# Revit family: Access_Flooring-FreeAxez-Border-L_Type
name_source: partatom
category: Specialty Equipment
units: mm (PartAtom-declared; Revit-internal decimal feet)

## family parameters
Always vertical = Yes
Classification Number = 23.35.50.27.14
Cut with Voids When Loaded = No
Enable Cutting in Views = No
Maintain Annotation Orientation = No
Part Type = Normal
Room Calculation Point = No
Round Connector Dimension = Use Diameter
Shared = No
Work Plane-Based = No

## types (2) — shared parameters
Default Elevation = 0' - 0"
Depth = 0' - 4 17/32"
Disclaimer = Your use of file(s) issued by FreeAxez, LLC confirms your acceptance of the following terms:  i) This file(s) is uncontrolled.  ii) Drawings are issued from FreeAxez, LLC in PDF format: The PDF document contains the issued data. Any accompanying BIM, CAD, image, or supplementary support file(s) is issued for your information only. Where discrepancies arise, the PDF document will take priority.  iii) This file(s) is to assist you with your production of work commissioned by FreeAxez, LLC for FreeAxez, LLC for the current project only and is not to be reused or manipulated by you on other projects, nor is it to be shared outside your organization without our express written permission.  iv) Where this file(s) is a BIM/CAD file, it is not a complete representation of the project but should be considered to show the design in general arrangement only and should not be relied on for construction purposes. Not all areas have been fully modelled. This File(s) should be read in conjunction with relevant details, specification, codes, and regulations.  v) Where this file is a BIM/CAD file and the project is in design stage, it plus any associated views or support files are made available for information purposes only and shall be considered Work In Progress. It is shared as an uncontrolled document and as such is subject to change and is to be treated as not yet checked or verified for use outside of the design team. The user is not to rely upon the data and/or information contained therein.  vi) Where this file is a BIM/CAD file issued for construction, it plus any associated views or support files are made available for information purposes only and is shared as an uncontrolled document. The user is not to rely upon the data and/or information contained therein.  vii) Where this file is a BIM/CAD file that has been exported from our Revit model(s) and shared as DGN, DWG, IFC, NWC or similar file formats, FreeAxez, LLC does not warrant the accuracy or completeness of the data. In addition, the user is not to expect linework weights, styles, colors, symbols, and geo-locations to align with the original BIM data.  viii) The information contained herein may be based on data or drawings supplied to FreeAxez, LLC by other parties and whilst every effort has been made to ensure the validity of data, FreeAxez, LLC do not warrant the accuracy or completeness of the data contained therein. FreeAxez, LLC makes no representations or warranties, express or implied, regarding the accuracy or completeness of this data.  ix) To the maximum extent permitted by law FreeAxez, LLC disclaims all warranties whether express or implied, including without limitation, all warranties of merchantability, title, and fitness for purpose of this file(s), and the user assumes full responsibility for loss resulting from any errors, variants, defects, virus infections or omissions in the supplied data and or information, and the use of or inability to use the data.  If you do not accept these conditions, please contact us immediately.
Manufacturer = FreeAxez
Product Documentation Link = https://www.freeaxez.com
Product Page URL = https://www.freeaxez.com
URL = https://www.freeaxez.com
Width = 1' - 7 11/16"
zero-valued in all types: Cost

## per-type parameters (varying)
| type | Description | Height | Model |
| Gridd40 | Gridd40 L-Type Border | 0' - 1 9/16" | FA-4103 |
| Gridd70 | Gridd70 L-Type Border | 0' - 2 3/4" | FA-7103 |

## geometry (parser evidence)
native form markers: Sweep x2
no freeform markers — native parametric forms only
